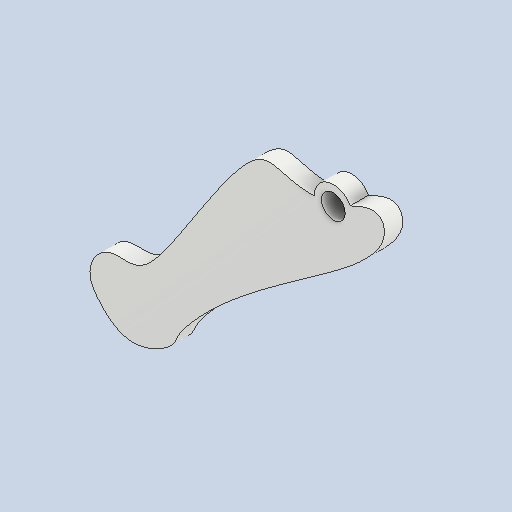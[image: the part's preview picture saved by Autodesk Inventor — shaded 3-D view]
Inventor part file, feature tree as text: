
AUTODESK INVENTOR PART (.ipt)
format: ipt  version: 2022 (Build 260153000, 153)  size: 114,176 bytes
history: native  units: in
note: dims shown in document units (in); Inventor stores cm internally (conversion verified against a paired STEP export)
features: other x3, sketch x1
ambient origin geometry x8: Origin, YZ Plane, XZ Plane, XY Plane, X Axis, Y Axis, Z Axis, Center Point
bodies: Solid1 (feature_tree)
feature tree (4):
  other  "Component36.ipt"
  other  "Solid1::Component36.ipt"
  other  "TaggingFeature1"
  sketch  "Sketch2"  dims[d0=0.3937in]
